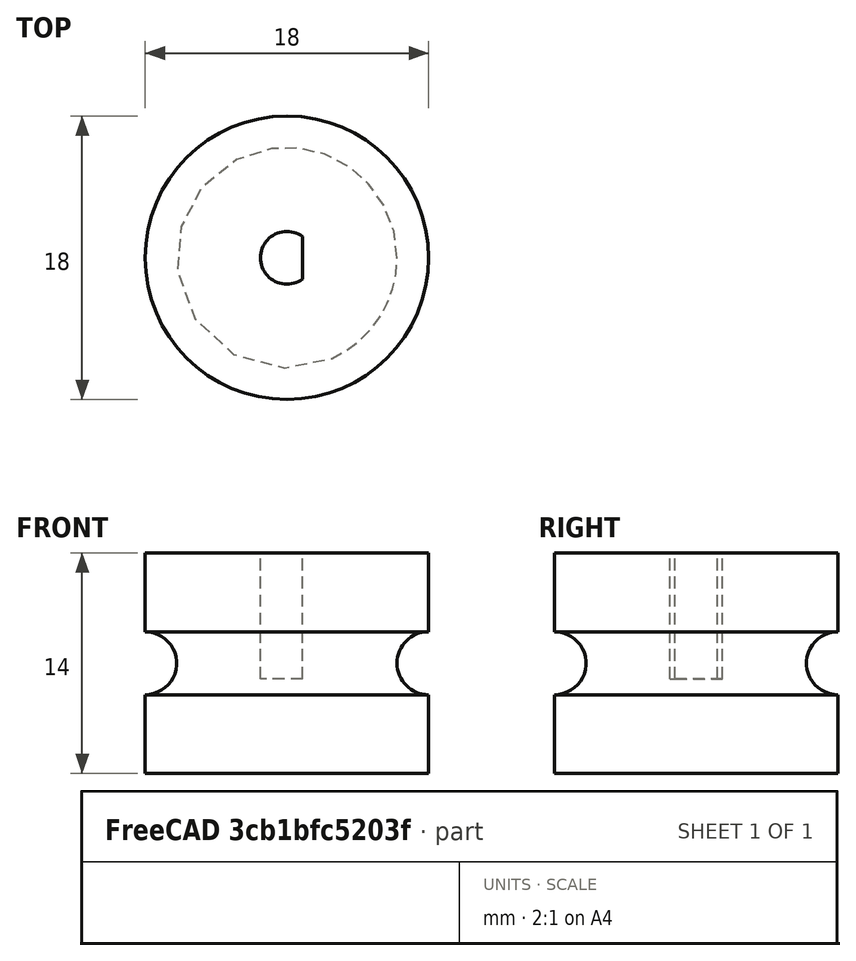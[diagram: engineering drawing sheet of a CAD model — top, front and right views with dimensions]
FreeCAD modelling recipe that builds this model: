
FCSTD DOCUMENT  (FreeCAD 0.16R6704 (Git))
Label: rueba pololu (1)
License: All rights reserved
LicenseURL: http://en.wikipedia.org/wiki/All_rights_reserved
objects: App::MeasureDistance×4, Part::Cut×3, Part::Cylinder×2, Part::Box×1, Part::Torus×1
note: 7 computed .brp shape members not serialized (recipe doc carries the construction recipe); baked Part::Feature solids carry a one-line shape summary decoded from their .brp

FEATURE [Part::Cylinder] Cylinder  label="rueda"
  Angle = 360
  Height = 14
  Radius = 9
FEATURE [Part::Cylinder] Cylinder001  label="eje"
  Angle = 360
  Height = 8
  Placement = pos=(0,0,15) rot=(0,0,1;0rad)
  Radius = 1.675
FEATURE [Part::Box] Box  label="D"
  Height = 8
  Length = 5
  Placement = pos=(1,-3,15) rot=(0,0,1;0rad)
  Width = 6
FEATURE [Part::Torus] Torus  label="anclaje"
  Angle1 = -180
  Angle2 = 180
  Angle3 = 360
  Placement = pos=(0,0,7) rot=(0,0,1;0rad)
  Radius1 = 9
  Radius2 = 2
FEATURE [Part::Cut] Cut  label="EJE + D"
  Base = -> Cylinder001
  Placement = pos=(0,0,-9) rot=(0,0,1;0rad)
  Tool = -> Box
FEATURE [Part::Cut] Cut001  label="RUEDA  + LLAGA"
  Base = -> Cylinder
  Tool = -> Torus
FEATURE [Part::Cut] Cut002  label="Rueda acabada"
  Base = -> Cut001
  Tool = -> Cut
FEATURE [App::MeasureDistance] Distance001  label="Distance: 3,90779 mm"
  Distance = 3.90779
  P1 = (-7.04408,3.09323,5.06351)
  P2 = (-7.2055,2.68815,8.9469)
FEATURE [App::MeasureDistance] Distance002  label="Distance: 14,0097 mm"
  Distance = 14.0097
  P1 = (-7.61469,-1.07799,0.0042942)
  P2 = (-7.50493,-1.69464,14)
FEATURE [App::MeasureDistance] Distance  label="Distance: 2,63651 mm"
  Distance = 2.63651
  P1 = (1,0.138228,14)
  P2 = (-1.63593,0.0827879,14)
FEATURE [App::MeasureDistance] Distance003  label="Distance: 3,32849 mm"
  Distance = 3.32849
  P1 = (0.211114,-1.63644,14)
  P2 = (0.0907252,1.68987,14)
